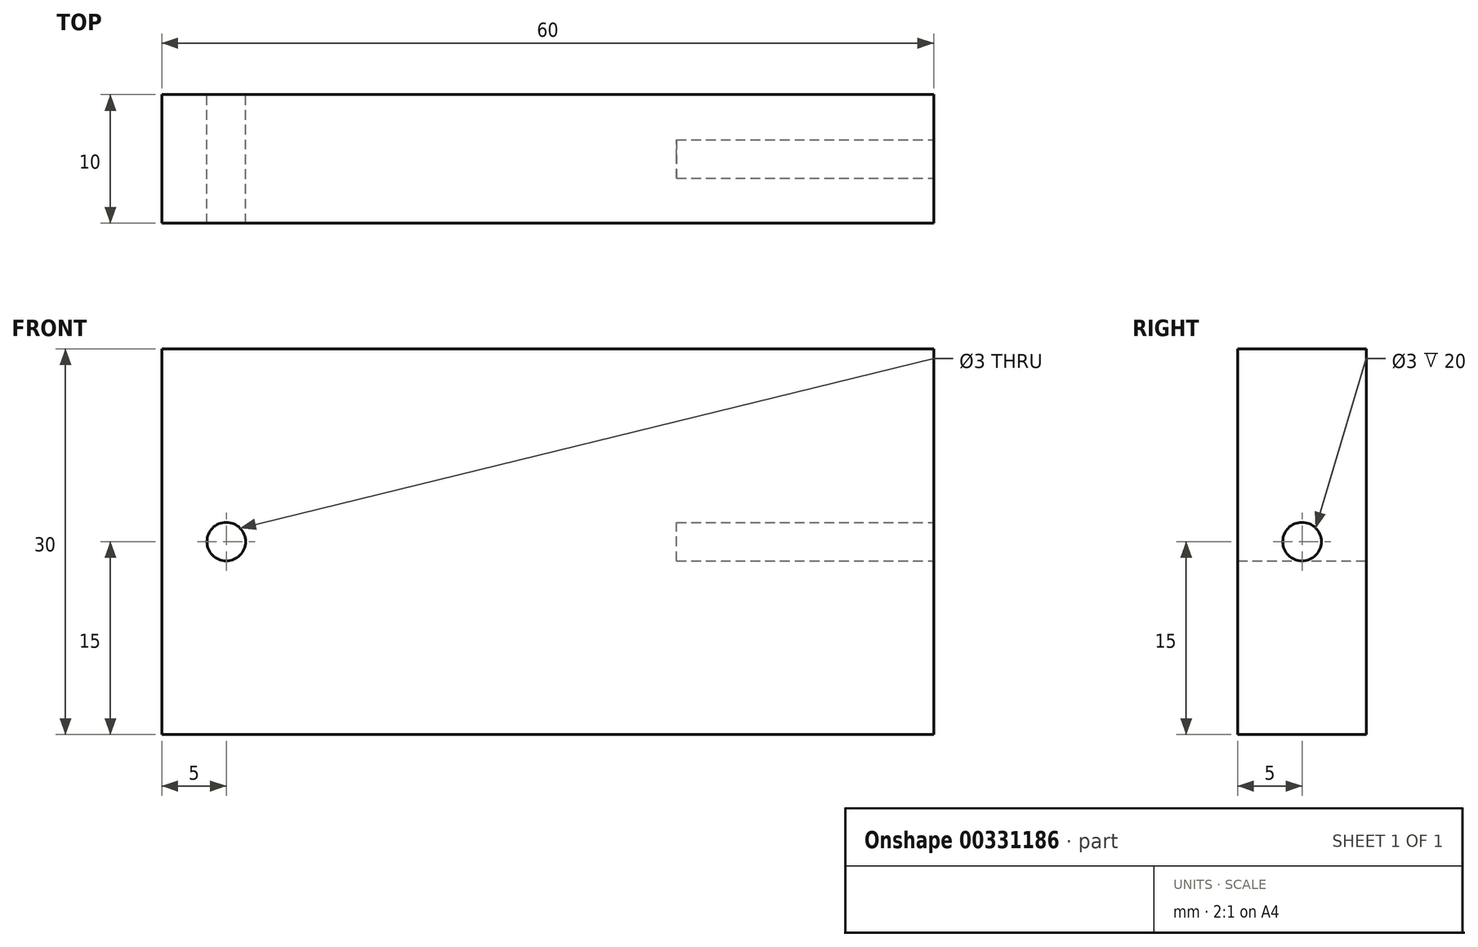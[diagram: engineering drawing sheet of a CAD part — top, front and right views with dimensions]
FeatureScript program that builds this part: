
annotation { "Feature Type Name" : "Feature", "Feature Type Description" : "" }
export const myFeature = defineFeature(function(context is Context, id is Id, definition is map)
    precondition{}
    {
        {
            var Q0;
            Q0=qCreatedBy(makeId("Front.planeOp"),FACE);
            var sketch = newSketch(context, id + "F0", { "sketchPlane" : qUnion([Q0])});
            skLineSegment(sketch, "E0.bottom", {"start": v(30, 15) * mm, "end": v(-30, 15) * mm});
            skLineSegment(sketch, "E0.top", {"start": v(30, -15) * mm, "end": v(-30, -15) * mm});
            skLineSegment(sketch, "E0.left", {"start": v(30, 15) * mm, "end": v(30, -15) * mm});
            skLineSegment(sketch, "E0.right", {"start": v(-30, 15) * mm, "end": v(-30, -15) * mm});
            skPoint(sketch, "E0.middle", {"position": v(0, 0) * mm});
            skLineSegment(sketch, "E1", {"start": v(-20, -15) * mm, "end": v(-20, 15) * mm});
            skPoint(sketch, "E2", {"position": v(-20, 0) * mm});
            skLineSegment(sketch, "E3", {"start": v(-30, 0) * mm, "end": v(-20, 0) * mm});
            skPoint(sketch, "E4", {"position": v(-25, 0) * mm});
            skCircle(sketch, "E5", {"center": v(-25, 0) * mm, "radius": 1.5 * mm});
            skSolve(sketch);
        }
        {
            var Q0;
            Q0=makeQuery(id+"F0.imprint","IMPRINT",FACE,{"disambiguationData":[TD([[makeQuery(id+"F0.imprint","IMPRINT",EDGE,{"derivedFrom":sQuery(id+"F0.wireOp",EDGE,"E0.bottom")}),1.0]])]});
            var Q1;
            {var subQ1=sQuery(id+"F0.wireOp",EDGE,"E0.right");var subQ6=sQuery(id+"F0.wireOp",EDGE,"E0.bottom");var subQ9=makeQuery(id+"F0.imprint","INTERSECT",VERTEX,{"derivedFrom":[subQ6,subQ1]});Q1=makeQuery(id+"F0.imprint","IMPRINT",FACE,{"disambiguationData":[TD([[makeQuery(id+"F0.imprint","IMPRINT",EDGE,{"disambiguationData":[TD([[subQ9,1.0]])],"derivedFrom":subQ6}),1.0]])]});}
            var Q2;
            {var subQ1=sQuery(id+"F0.wireOp",EDGE,"E0.right");var subQ6=sQuery(id+"F0.wireOp",EDGE,"E0.top");var subQ9=makeQuery(id+"F0.imprint","INTERSECT",VERTEX,{"derivedFrom":[subQ6,subQ1]});Q2=makeQuery(id+"F0.imprint","IMPRINT",FACE,{"disambiguationData":[TD([[makeQuery(id+"F0.imprint","IMPRINT",EDGE,{"disambiguationData":[TD([[subQ9,1.0]])],"derivedFrom":subQ6}),-1.0]])]});}
            extrude(context, id + "F1", {"entities" : qUnion([Q0, Q1, Q2]), "depth" : 10 * mm});
        }
        {
            var Q0;
            Q0=makeQuery(id+"F1.opExtrude","SWEPT_FACE",FACE,{"disambiguationData":[OSD([sQuery(id+"F0.wireOp",EDGE,"E0.left")])]});
            var sketch = newSketch(context, id + "F2", { "sketchPlane" : qUnion([Q0])});
            skLineSegment(sketch, "E6", {"start": v(-5, 0) * mm, "end": v(-3.5, 0) * mm});
            skPoint(sketch, "E7", {"position": v(-5, 0) * mm});
            skCircle(sketch, "E8", {"center": v(-5, 0) * mm, "radius": 1.5 * mm});
            skPoint(sketch, "E9.orphan", {"position": v(-10, 0) * mm});
            skPoint(sketch, "E10.orphan", {"position": v(0, 0) * mm});
            skSolve(sketch);
        }
        {
            var Q0;
            Q0=makeQuery(id+"F2.imprint","IMPRINT",FACE,{"disambiguationData":[TD([[makeQuery(id+"F2.imprint","IMPRINT",EDGE,{"derivedFrom":sQuery(id+"F2.wireOp",EDGE,"E8")}),1.0]])]});
            var Q1;
            Q1=sQuery(id+"F2.wireOp",EDGE,"E8");
            extrude(context, id + "F3", {"entities" : qUnion([Q0]), "operationType" : NewBodyOperationType.REMOVE, "surfaceEntities" : qUnion([Q1]), "oppositeDirection" : true, "depth" : 20 * mm});
        }
    });
